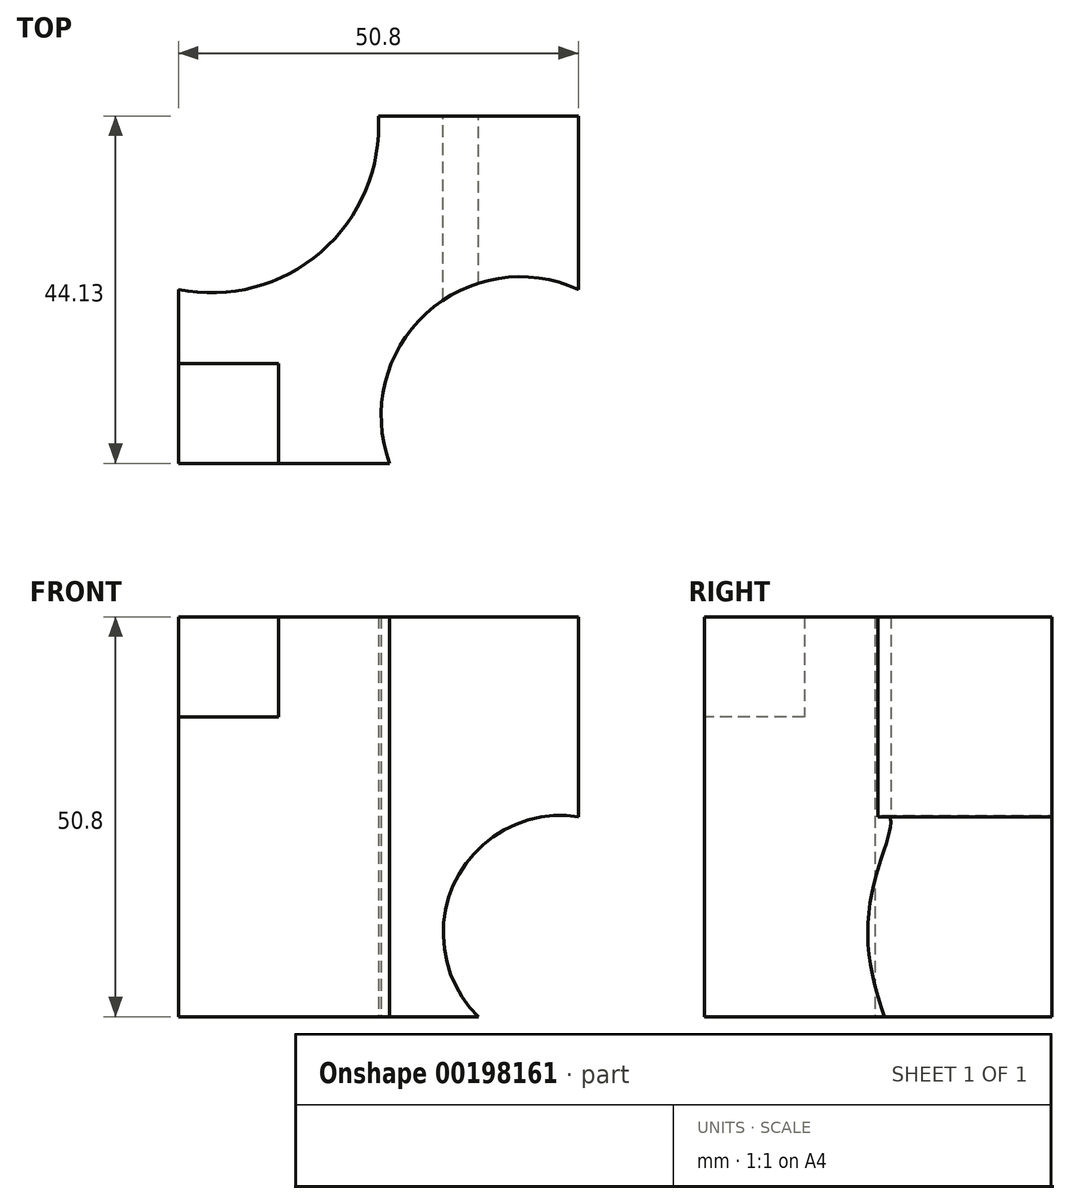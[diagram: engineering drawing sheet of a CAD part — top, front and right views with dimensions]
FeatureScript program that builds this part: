
annotation { "Feature Type Name" : "Feature", "Feature Type Description" : "" }
export const myFeature = defineFeature(function(context is Context, id is Id, definition is map)
    precondition{}
    {
        {
            var Q0;
            Q0=qCreatedBy(makeId("Top.planeOp"),FACE);
            var sketch = newSketch(context, id + "F0", { "sketchPlane" : qUnion([Q0])});
            skLineSegment(sketch, "E0.bottom", {"start": v(-3.4, 22.53) * mm, "end": v(22, 22.53) * mm});
            skLineSegment(sketch, "E0.top", {"start": v(-28.8, -21.6) * mm, "end": v(-2, -21.6) * mm});
            skLineSegment(sketch, "E0.left", {"start": v(-28.8, 0.46) * mm, "end": v(-28.8, -21.6) * mm});
            skLineSegment(sketch, "E0.right", {"start": v(22, 22.53) * mm, "end": v(22, 0.46) * mm});
            skArc(sketch, "E1", {"start": v(-28.8, 0.46) * mm, "mid": v(-10.68, 5.26) * mm, "end": v(-3.4, 22.53) * mm});
            skArc(sketch, "E2", {"start": v(22, 0.46) * mm, "mid": v(2.64, -2.57) * mm, "end": v(-2, -21.6) * mm});
            skPoint(sketch, "E3.orphan", {"position": v(-28.8, 22.53) * mm});
            skPoint(sketch, "E4.orphan", {"position": v(22, -21.6) * mm});
            skSolve(sketch);
        }
        {
            var Q0;
            Q0=makeQuery(id+"F0.imprint","IMPRINT",FACE,{"disambiguationData":[TD([[makeQuery(id+"F0.imprint","IMPRINT",EDGE,{"derivedFrom":sQuery(id+"F0.wireOp",EDGE,"E0.bottom")}),-1.0]])]});
            extrude(context, id + "F1", {"entities" : qUnion([Q0]), "depth" : 50.8 * mm});
        }
        {
            var Q0;
            Q0=makeQuery(id+"F1.opExtrude","SWEPT_FACE",FACE,{"disambiguationData":[OSD([sQuery(id+"F0.wireOp",EDGE,"E0.left")])]});
            var sketch = newSketch(context, id + "F2", { "sketchPlane" : qUnion([Q0])});
            skLineSegment(sketch, "E5.bottom", {"start": v(8.9, 50.8) * mm, "end": v(21.6, 50.8) * mm});
            skLineSegment(sketch, "E5.top", {"start": v(8.9, 38.1) * mm, "end": v(21.6, 38.1) * mm});
            skLineSegment(sketch, "E5.left", {"start": v(8.9, 50.8) * mm, "end": v(8.9, 38.1) * mm});
            skLineSegment(sketch, "E5.right", {"start": v(21.6, 50.8) * mm, "end": v(21.6, 38.1) * mm});
            skSolve(sketch);
        }
        {
            var Q0;
            Q0 = qSketchRegion(id + "F2", true);
            extrude(context, id + "F3", {"entities" : qUnion([Q0]), "operationType" : NewBodyOperationType.REMOVE, "oppositeDirection" : true, "depth" : 12.7 * mm});
        }
        {
            var Q0;
            Q0=makeQuery(id+"F1.opExtrude","SWEPT_FACE",FACE,{"disambiguationData":[OSD([sQuery(id+"F0.wireOp",EDGE,"E0.bottom")])]});
            var sketch = newSketch(context, id + "F4", { "sketchPlane" : qUnion([Q0])});
            skArc(sketch, "E6", {"start": v(-9.3, 0) * mm, "mid": v(-6.4, 17.32) * mm, "end": v(-22, 25.4) * mm});
            skLineSegment(sketch, "E7", {"start": v(-22, 0) * mm, "end": v(-9.3, 0) * mm});
            skLineSegment(sketch, "E8", {"start": v(-22, 25.4) * mm, "end": v(-22, 0) * mm});
            skSolve(sketch);
        }
        {
            var Q0;
            Q0=makeQuery(id+"F4.imprint","IMPRINT",FACE,{"disambiguationData":[TD([[makeQuery(id+"F4.imprint","IMPRINT",EDGE,{"derivedFrom":sQuery(id+"F4.wireOp",EDGE,"E6")}),1.0]])]});
            extrude(context, id + "F5", {"entities" : qUnion([Q0]), "operationType" : NewBodyOperationType.REMOVE, "oppositeDirection" : true, "depth" : 25.4 * mm});
        }
    });
